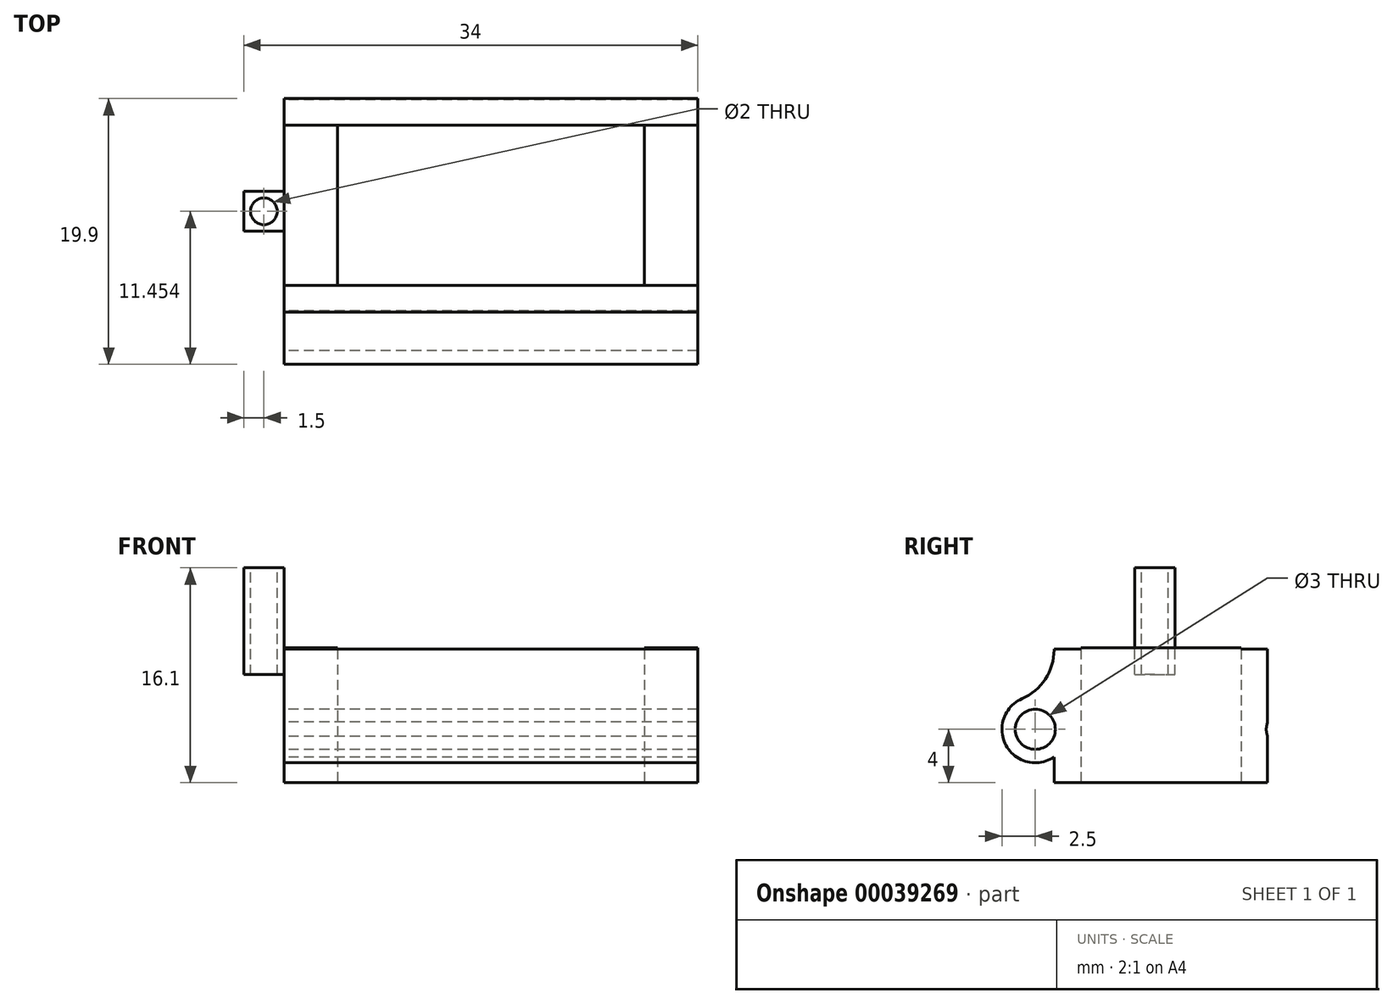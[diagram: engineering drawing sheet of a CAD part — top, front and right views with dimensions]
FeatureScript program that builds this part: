
annotation { "Feature Type Name" : "Feature", "Feature Type Description" : "" }
export const myFeature = defineFeature(function(context is Context, id is Id, definition is map)
    precondition{}
    {
        {
            var Q0;
            Q0=qCreatedBy(makeId("Top.planeOp"),FACE);
            var sketch = newSketch(context, id + "F0", { "sketchPlane" : qUnion([Q0])});
            skLineSegment(sketch, "E0.rect.bottom", {"start": v(11.5, -6) * mm, "end": v(-11.5, -6) * mm});
            skLineSegment(sketch, "E0.rect.top", {"start": v(11.5, 6) * mm, "end": v(-11.5, 6) * mm});
            skLineSegment(sketch, "E0.rect.left", {"start": v(11.5, -6) * mm, "end": v(11.5, 6) * mm});
            skLineSegment(sketch, "E0.rect.right", {"start": v(-11.5, -6) * mm, "end": v(-11.5, 6) * mm});
            skPoint(sketch, "E0.rect.middle", {"position": v(0, 0) * mm});
            skLineSegment(sketch, "E1.rect.bottom", {"start": v(15.5, -8) * mm, "end": v(-15.5, -8) * mm});
            skLineSegment(sketch, "E1.rect.top", {"start": v(15.5, 8) * mm, "end": v(-15.5, 8) * mm});
            skLineSegment(sketch, "E1.rect.left", {"start": v(15.5, -8) * mm, "end": v(15.5, 8) * mm});
            skLineSegment(sketch, "E1.rect.right", {"start": v(-15.5, -8) * mm, "end": v(-15.5, 8) * mm});
            skSolve(sketch);
        }
        {
            var Q0;
            Q0=makeQuery(id+"F0.imprint","IMPRINT",FACE,{"disambiguationData":[TD([[makeQuery(id+"F0.imprint","IMPRINT",EDGE,{"derivedFrom":sQuery(id+"F0.wireOp",EDGE,"E0.rect.bottom")}),1.0]])]});
            extrude(context, id + "F1", {"entities" : qUnion([Q0]), "depth" : 10 * mm});
        }
        {
            var Q0;
            Q0=makeQuery(id+"F1.opExtrude","SWEPT_FACE",FACE,{"disambiguationData":[OSD([sQuery(id+"F0.wireOp",EDGE,"E1.rect.right")])]});
            var sketch = newSketch(context, id + "F2", { "sketchPlane" : qUnion([Q0])});
            skLineSegment(sketch, "E2", {"start": v(8, 10) * mm, "end": v(8, 4) * mm});
            skLineSegment(sketch, "E3", {"start": v(8, 4) * mm, "end": v(9.4, 4) * mm});
            skCircle(sketch, "E4", {"center": v(9.4, 4) * mm, "radius": 1.5 * mm});
            skCircle(sketch, "E5", {"center": v(9.4, 4) * mm, "radius": 2.5 * mm});
            skLineSegment(sketch, "E6", {"start": v(8, 4) * mm, "end": v(-8, 4) * mm});
            skLineSegment(sketch, "E7", {"start": v(-8, 4) * mm, "end": v(-9.4, 4) * mm});
            skCircle(sketch, "E8", {"center": v(-9.4, 4) * mm, "radius": 1.5 * mm});
            skCircle(sketch, "E9", {"center": v(-9.4, 4) * mm, "radius": 2.5 * mm});
            skSolve(sketch);
        }
        {
            var Q0;
            Q0=makeQuery(id+"F1.opExtrude","CAP_FACE",FACE,{"disambiguationData":[OSD([sQuery(id+"F0.wireOp",EDGE,"E0.rect.bottom"),sQuery(id+"F0.wireOp",EDGE,"E0.rect.top"),sQuery(id+"F0.wireOp",EDGE,"E0.rect.left"),sQuery(id+"F0.wireOp",EDGE,"E0.rect.right"),sQuery(id+"F0.wireOp",EDGE,"E1.rect.bottom"),sQuery(id+"F0.wireOp",EDGE,"E1.rect.top"),sQuery(id+"F0.wireOp",EDGE,"E1.rect.left"),sQuery(id+"F0.wireOp",EDGE,"E1.rect.right")])],"isStart":false});
            var sketch = newSketch(context, id + "F3", { "sketchPlane" : qUnion([Q0])});
            skLineSegment(sketch, "E10", {"start": v(-11.5, 6) * mm, "end": v(-15.5, 6) * mm});
            skLineSegment(sketch, "E11", {"start": v(-15.5, 6) * mm, "end": v(-15.5, -6) * mm});
            skLineSegment(sketch, "E12", {"start": v(-15.5, -6) * mm, "end": v(-11.5, -6) * mm});
            skLineSegment(sketch, "E13", {"start": v(11.5, 6) * mm, "end": v(15.5, 6) * mm});
            skLineSegment(sketch, "E14", {"start": v(15.5, 6) * mm, "end": v(15.5, -6) * mm});
            skLineSegment(sketch, "E15", {"start": v(15.5, -6) * mm, "end": v(11.5, -6) * mm});
            skSolve(sketch);
        }
        {
            var Q0;
            Q0=makeQuery(id+"F3.imprint","IMPRINT",FACE,{"disambiguationData":[TD([[makeQuery(id+"F3.imprint","IMPRINT",EDGE,{"derivedFrom":sQuery(id+"F3.wireOp",EDGE,"E13")}),-1.0]])]});
            var Q1;
            Q1=makeQuery(id+"F3.imprint","IMPRINT",FACE,{"disambiguationData":[TD([[makeQuery(id+"F3.imprint","IMPRINT",EDGE,{"derivedFrom":sQuery(id+"F3.wireOp",EDGE,"E10")}),1.0]])]});
            extrude(context, id + "F4", {"entities" : qUnion([Q0, Q1]), "operationType" : NewBodyOperationType.ADD, "depth" : 0.1 * mm});
        }
        {
            var Q0;
            {var subQ3=sQuery(id+"F2.wireOp",EDGE,"E2");var subQ5=sQuery(id+"F2.wireOp",EDGE,"E5");var subQ7=makeQuery(id+"F2.imprint","INTERSECT",VERTEX,{"derivedFrom":[subQ3,subQ5]});Q0=makeQuery(id+"F2.imprint","IMPRINT",FACE,{"disambiguationData":[TD([[makeQuery(id+"F2.imprint","IMPRINT",EDGE,{"disambiguationData":[TD([[subQ7,-1.0]])],"derivedFrom":subQ3}),1.0]])]});}
            var Q1;
            {var subQ0=makeQuery(id+"F1.opExtrude","SWEPT_EDGE",EDGE,{"disambiguationData":[OSD([sQuery(id+"F0.wireOp",EDGE,"E1.rect.top"),sQuery(id+"F0.wireOp",EDGE,"E1.rect.right")])]});var subQ1=sQuery(id+"F2.wireOp",EDGE,"E8");var subQ2=makeQuery(id+"F2.imprint","INTERSECT",VERTEX,{"disambiguationData":[OD(0.0)],"derivedFrom":[subQ0,subQ1]});Q1=makeQuery(id+"F2.imprint","IMPRINT",FACE,{"disambiguationData":[TD([[makeQuery(id+"F2.imprint","IMPRINT",EDGE,{"disambiguationData":[TD([[subQ2,-1.0]])],"derivedFrom":subQ1}),-1.0]])]});}
            extrude(context, id + "F5", {"entities" : qUnion([Q0, Q1]), "operationType" : NewBodyOperationType.ADD, "oppositeDirection" : true, "depth" : 31 * mm});
        }
        {
            var Q0;
            {var subQ1=sQuery(id+"F2.wireOp",EDGE,"E4");var subQ3=sQuery(id+"F2.wireOp",EDGE,"E2");var subQ5=makeQuery(id+"F2.imprint","INTERSECT",VERTEX,{"derivedFrom":[subQ3,subQ1]});Q0=makeQuery(id+"F2.imprint","IMPRINT",FACE,{"disambiguationData":[TD([[makeQuery(id+"F2.imprint","IMPRINT",EDGE,{"disambiguationData":[TD([[subQ5,-1.0]])],"derivedFrom":subQ1}),1.0]])]});}
            var Q1;
            {var subQ1=sQuery(id+"F2.wireOp",EDGE,"E4");var subQ3=sQuery(id+"F2.wireOp",EDGE,"E6");var subQ5=makeQuery(id+"F2.imprint","INTERSECT",VERTEX,{"derivedFrom":[subQ1,subQ3]});Q1=makeQuery(id+"F2.imprint","IMPRINT",FACE,{"disambiguationData":[TD([[makeQuery(id+"F2.imprint","IMPRINT",EDGE,{"disambiguationData":[TD([[subQ5,-1.0]])],"derivedFrom":subQ1}),1.0]])]});}
            var Q2;
            {var subQ1=sQuery(id+"F2.wireOp",EDGE,"E8");var subQ3=sQuery(id+"F2.wireOp",EDGE,"E6");var subQ5=makeQuery(id+"F2.imprint","INTERSECT",VERTEX,{"derivedFrom":[subQ3,subQ1]});Q2=makeQuery(id+"F2.imprint","IMPRINT",FACE,{"disambiguationData":[TD([[makeQuery(id+"F2.imprint","IMPRINT",EDGE,{"disambiguationData":[TD([[subQ5,-1.0]])],"derivedFrom":subQ3}),-1.0]])]});}
            var Q3;
            {var subQ0=sQuery(id+"F2.wireOp",EDGE,"E8");var subQ3=sQuery(id+"F2.wireOp",EDGE,"E6");var subQ4=makeQuery(id+"F2.imprint","INTERSECT",VERTEX,{"derivedFrom":[subQ3,subQ0]});Q3=makeQuery(id+"F2.imprint","IMPRINT",FACE,{"disambiguationData":[TD([[makeQuery(id+"F2.imprint","IMPRINT",EDGE,{"disambiguationData":[TD([[subQ4,-1.0]])],"derivedFrom":subQ3}),1.0]])]});}
            extrude(context, id + "F6", {"entities" : qUnion([Q0, Q1, Q2, Q3]), "operationType" : NewBodyOperationType.REMOVE, "oppositeDirection" : true, "depth" : 50 * mm});
        }
        {
            var Q0;
            Q0=makeQuery(id+"F5.opExtrude","SWEPT_EDGE",EDGE,{"disambiguationData":[OSD([sQuery(id+"F0.wireOp",EDGE,"E1.rect.bottom"),sQuery(id+"F0.wireOp",EDGE,"E1.rect.right"),sQuery(id+"F2.wireOp",EDGE,"E5")])]});
            var Q1;
            Q1=makeQuery(id+"F5.opExtrude","SWEPT_EDGE",EDGE,{"disambiguationData":[OSD([sQuery(id+"F2.wireOp",EDGE,"E2"),sQuery(id+"F2.wireOp",EDGE,"E5")])]});
            var Q2;
            {var subQ0=sQuery(id+"F0.wireOp",EDGE,"E1.rect.top");var subQ1=sQuery(id+"F0.wireOp",EDGE,"E1.rect.right");var subQ2=sQuery(id+"F2.wireOp",EDGE,"E9");Q2=makeQuery(id+"F5.opExtrude","SWEPT_EDGE",EDGE,{"disambiguationData":[OSD([subQ0,subQ1,subQ2]),TDD([makeQuery(id+"F2.imprint","INTERSECT",VERTEX,{"disambiguationData":[OD(1.0)],"derivedFrom":[makeQuery(id+"F1.opExtrude","SWEPT_EDGE",EDGE,{"disambiguationData":[OSD([subQ0,subQ1])]}),subQ2]})])]});}
            var Q3;
            {var subQ0=sQuery(id+"F0.wireOp",EDGE,"E1.rect.top");var subQ1=sQuery(id+"F0.wireOp",EDGE,"E1.rect.right");var subQ2=sQuery(id+"F2.wireOp",EDGE,"E9");Q3=makeQuery(id+"F5.opExtrude","SWEPT_EDGE",EDGE,{"disambiguationData":[OSD([subQ0,subQ1,subQ2]),TDD([makeQuery(id+"F2.imprint","INTERSECT",VERTEX,{"disambiguationData":[OD(0.0)],"derivedFrom":[makeQuery(id+"F1.opExtrude","SWEPT_EDGE",EDGE,{"disambiguationData":[OSD([subQ0,subQ1])]}),subQ2]})])]});}
            fillet(context, id + "F7", {"entities" : qUnion([Q0, Q1, Q2, Q3]), "radius" : 4 * mm, "tangentPropagation" : true, "allowEdgeOverflow" : false});
        }
        {
            var Q0;
            {var subQ0=sQuery(id+"F0.wireOp",EDGE,"E1.rect.right");Q0=makeQuery(id+"F5.boolean.opBoolean","MERGE",FACE,{"derivedFrom":[makeQuery(id+"F4.boolean.opBoolean","MERGE",FACE,{"derivedFrom":[makeQuery(id+"F1.opExtrude","SWEPT_FACE",FACE,{"disambiguationData":[OSD([subQ0])]}),makeQuery(id+"F4.opExtrude","SWEPT_FACE",FACE,{"disambiguationData":[OSD([sQuery(id+"F3.wireOp",EDGE,"E11")])]})]}),makeQuery(id+"F5.opExtrude","CAP_FACE",FACE,{"disambiguationData":[OSD([sQuery(id+"F0.wireOp",EDGE,"E1.rect.bottom"),subQ0,sQuery(id+"F2.wireOp",EDGE,"E2"),sQuery(id+"F2.wireOp",EDGE,"E4"),sQuery(id+"F2.wireOp",EDGE,"E5")])],"isStart":true}),makeQuery(id+"F5.opExtrude","CAP_FACE",FACE,{"disambiguationData":[OSD([sQuery(id+"F0.wireOp",EDGE,"E1.rect.top"),subQ0,sQuery(id+"F2.wireOp",EDGE,"E8"),sQuery(id+"F2.wireOp",EDGE,"E9")])],"isStart":true})]});}
            var sketch = newSketch(context, id + "F8", { "sketchPlane" : qUnion([Q0])});
            skPoint(sketch, "E16.rect.middle", {"position": v(0, 10.1) * mm});
            skLineSegment(sketch, "E17.rect.bottom", {"start": v(1.95, 8.1) * mm, "end": v(-1.05, 8.1) * mm});
            skLineSegment(sketch, "E17.rect.top", {"start": v(1.95, 12.1) * mm, "end": v(-1.05, 12.1) * mm});
            skLineSegment(sketch, "E17.rect.left", {"start": v(1.95, 8.1) * mm, "end": v(1.95, 12.1) * mm});
            skLineSegment(sketch, "E17.rect.right", {"start": v(-1.05, 8.1) * mm, "end": v(-1.05, 12.1) * mm});
            skPoint(sketch, "E17.rect.middle", {"position": v(0.45, 10.1) * mm});
            skSolve(sketch);
        }
        {
            var Q0;
            {var subQ5=sQuery(id+"F8.wireOp",EDGE,"E17.rect.top");Q0=makeQuery(id+"F8.imprint","IMPRINT",FACE,{"disambiguationData":[TD([[makeQuery(id+"F8.imprint","IMPRINT",EDGE,{"derivedFrom":subQ5}),1.0]])]});}
            var Q1;
            {var subQ3=sQuery(id+"F8.wireOp",EDGE,"E17.rect.bottom");Q1=makeQuery(id+"F8.imprint","IMPRINT",FACE,{"disambiguationData":[TD([[makeQuery(id+"F8.imprint","IMPRINT",EDGE,{"derivedFrom":subQ3}),-1.0]])]});}
            extrude(context, id + "F9", {"entities" : qUnion([Q0, Q1]), "operationType" : NewBodyOperationType.ADD, "depth" : 3 * mm});
        }
        {
            var Q0;
            Q0=makeQuery(id+"F9.opExtrude","SWEPT_FACE",FACE,{"disambiguationData":[OSD([sQuery(id+"F8.wireOp",EDGE,"E17.rect.top")])]});
            var sketch = newSketch(context, id + "F10", { "sketchPlane" : qUnion([Q0])});
            skCircle(sketch, "E18", {"center": v(-17, -0.45) * mm, "radius": 1 * mm});
            skPoint(sketch, "E18.centerSnap0", {"position": v(-17, 1.05) * mm});
            skPoint(sketch, "E18.centerSnap1", {"position": v(-18.5, -0.45) * mm});
            skSolve(sketch);
        }
        {
            var Q0;
            Q0=makeQuery(id+"F10.imprint","IMPRINT",FACE,{"disambiguationData":[TD([[makeQuery(id+"F10.imprint","IMPRINT",EDGE,{"derivedFrom":sQuery(id+"F10.wireOp",EDGE,"E18")}),1.0]])]});
            extrude(context, id + "F11", {"entities" : qUnion([Q0]), "operationType" : NewBodyOperationType.REMOVE, "oppositeDirection" : true, "depth" : 5 * mm});
        }
        {
            var Q0;
            Q0=makeQuery(id+"F9.opExtrude","SWEPT_FACE",FACE,{"disambiguationData":[OSD([sQuery(id+"F8.wireOp",EDGE,"E17.rect.top")])]});
            extrude(context, id + "F12", {"entities" : qUnion([Q0]), "operationType" : NewBodyOperationType.ADD, "depth" : 4 * mm});
        }
    });
